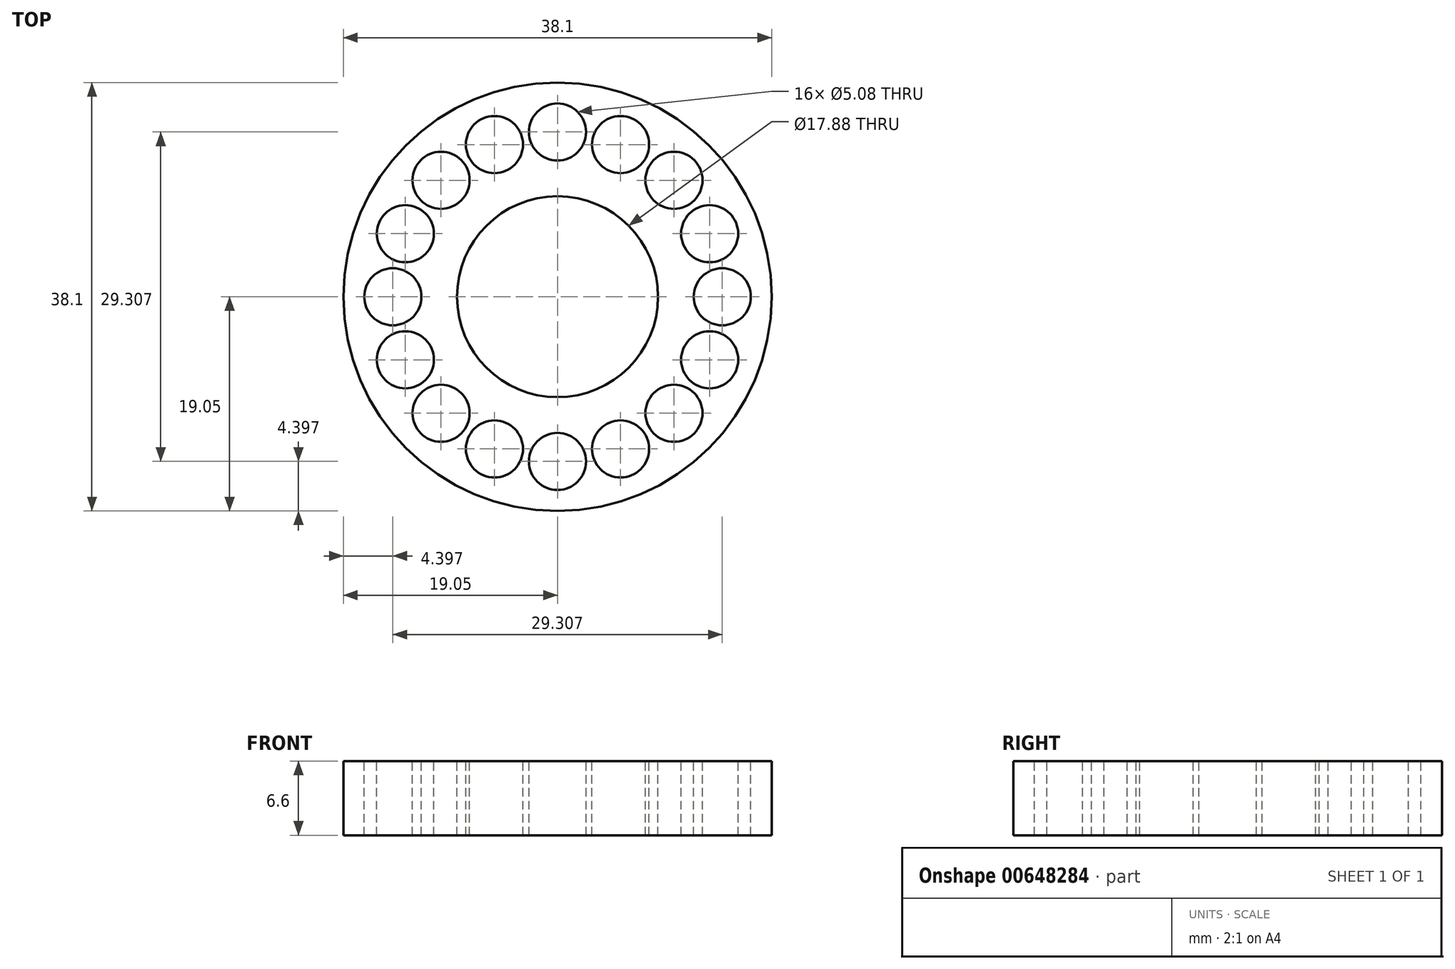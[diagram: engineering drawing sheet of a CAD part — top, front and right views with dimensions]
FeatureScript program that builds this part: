
annotation { "Feature Type Name" : "Feature", "Feature Type Description" : "" }
export const myFeature = defineFeature(function(context is Context, id is Id, definition is map)
    precondition{}
    {
        {
            var Q0;
            Q0=qCreatedBy(makeId("Top.planeOp"),FACE);
            var sketch = newSketch(context, id + "F0", { "sketchPlane" : qUnion([Q0])});
            skCircle(sketch, "E0", {"center": v(0, 0) * mm, "radius": 8.94 * mm});
            skCircle(sketch, "E1", {"center": v(0, 0) * mm, "radius": 19.05 * mm});
            skCircle(sketch, "E2", {"center": v(-14.65, 0) * mm, "radius": 2.54 * mm});
            skCircle(sketch, "E3.1.0", {"center": v(-10.36, 10.36) * mm, "radius": 2.54 * mm});
            skCircle(sketch, "E3.2.0", {"center": v(0, 14.65) * mm, "radius": 2.54 * mm});
            skCircle(sketch, "E4.1.0", {"center": v(10.36, 10.36) * mm, "radius": 2.54 * mm});
            skCircle(sketch, "E4.2.0", {"center": v(14.65, 0) * mm, "radius": 2.54 * mm});
            skCircle(sketch, "E5.1.0", {"center": v(10.36, -10.36) * mm, "radius": 2.5 * mm});
            skCircle(sketch, "E5.2.0", {"center": v(0, -14.65) * mm, "radius": 2.54 * mm});
            skCircle(sketch, "E6.1.0", {"center": v(-10.36, -10.36) * mm, "radius": 2.54 * mm});
            skCircle(sketch, "E7.1.0", {"center": v(-5.6, 13.54) * mm, "radius": 2.54 * mm});
            skCircle(sketch, "E8.1.0", {"center": v(5.6, 13.54) * mm, "radius": 2.54 * mm});
            skCircle(sketch, "E9.1.0", {"center": v(13.54, 5.6) * mm, "radius": 2.54 * mm});
            skCircle(sketch, "E10.1.0", {"center": v(13.54, -5.6) * mm, "radius": 2.54 * mm});
            skCircle(sketch, "E10.2.0", {"center": v(10.36, -10.36) * mm, "radius": 2.54 * mm});
            skCircle(sketch, "E11.1.0", {"center": v(5.6, -13.54) * mm, "radius": 2.54 * mm});
            skCircle(sketch, "E12.1.0", {"center": v(-5.6, -13.54) * mm, "radius": 2.54 * mm});
            skCircle(sketch, "E13.1.0", {"center": v(-13.54, -5.6) * mm, "radius": 2.54 * mm});
            skCircle(sketch, "E14.1.0", {"center": v(-13.54, 5.6) * mm, "radius": 2.54 * mm});
            skSolve(sketch);
        }
        {
            var Q0;
            Q0 = qSketchRegion(id + "F0", true);
            extrude(context, id + "F1", {"entities" : qUnion([Q0]), "flatOperationType" : FlatOperationType.REMOVE, "oppositeDirection" : true, "depth" : 6.6 * mm, "offsetDistance" : 25.4 * mm, "domain" : OperationDomain.MODEL});
        }
    });
